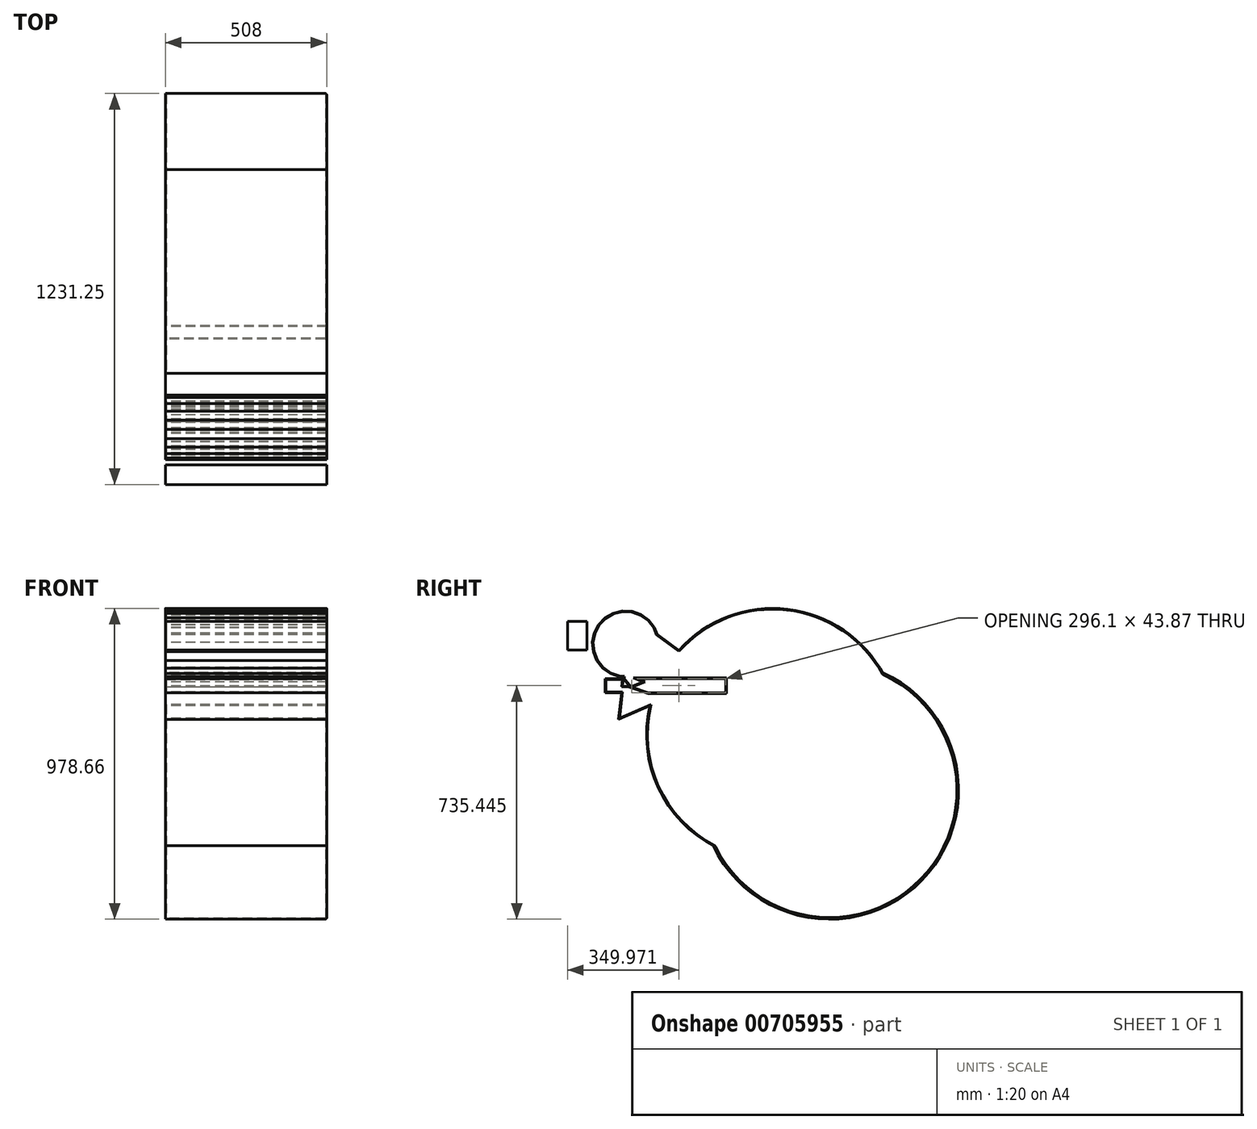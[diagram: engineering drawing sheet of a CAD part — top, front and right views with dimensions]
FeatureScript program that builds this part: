
annotation { "Feature Type Name" : "Feature", "Feature Type Description" : "" }
export const myFeature = defineFeature(function(context is Context, id is Id, definition is map)
    precondition{}
    {
        {
            var Q0;
            Q0=qCreatedBy(makeId("Right.planeOp"),FACE);
            var sketch = newSketch(context, id + "F0", { "sketchPlane" : qUnion([Q0])});
            skLineSegment(sketch, "E0.bottom", {"start": v(-498.02, 313) * mm, "end": v(-436.5, 313) * mm});
            skLineSegment(sketch, "E0.top", {"start": v(-498.02, 222.69) * mm, "end": v(-436.5, 222.69) * mm});
            skLineSegment(sketch, "E0.left", {"start": v(-498.02, 313) * mm, "end": v(-498.02, 222.69) * mm});
            skLineSegment(sketch, "E0.right", {"start": v(-436.5, 313) * mm, "end": v(-436.5, 222.69) * mm});
            skPoint(sketch, "E0.middle", {"position": v(-467.26, 267.84) * mm});
            skLineSegment(sketch, "E1.bottom", {"start": v(-379.5, 132.56) * mm, "end": v(0, 132.56) * mm});
            skLineSegment(sketch, "E1.top", {"start": v(-379.5, 88.69) * mm, "end": v(0, 88.69) * mm});
            skLineSegment(sketch, "E1.left", {"start": v(-379.5, 132.56) * mm, "end": v(-379.5, 88.69) * mm});
            skLineSegment(sketch, "E1.right", {"start": v(0, 132.56) * mm, "end": v(0, 88.69) * mm});
            skLineSegment(sketch, "E2.bottom", {"start": v(-302.6, 108.21) * mm, "end": v(-302.6, 108.21) * mm});
            skLineSegment(sketch, "E2.top", {"start": v(-302.6, 124.93) * mm, "end": v(-302.6, 124.93) * mm});
            skLineSegment(sketch, "E2.left", {"start": v(-302.6, 108.21) * mm, "end": v(-302.6, 124.93) * mm});
            skLineSegment(sketch, "E2.right", {"start": v(-302.6, 108.21) * mm, "end": v(-302.6, 124.93) * mm});
            skLineSegment(sketch, "E3", {"start": v(-379.5, 110.62) * mm, "end": v(-336.08, 110.62) * mm});
            skLineSegment(sketch, "E4", {"start": v(-336.08, 110.62) * mm, "end": v(-349.65, 132.56) * mm});
            skLineSegment(sketch, "E5", {"start": v(-336.08, 110.62) * mm, "end": v(-302.6, 108.21) * mm});
            skLineSegment(sketch, "E6", {"start": v(-302.6, 108.21) * mm, "end": v(-322.51, 132.56) * mm});
            skLineSegment(sketch, "E7", {"start": v(-302.6, 108.21) * mm, "end": v(-243.8, 88.69) * mm});
            skLineSegment(sketch, "E8", {"start": v(-296.1, 106.05) * mm, "end": v(-228.43, 132.56) * mm});
            skLineSegment(sketch, "E9", {"start": v(-277.04, 113.52) * mm, "end": v(-167.81, 88.69) * mm});
            skCircle(sketch, "E10.cCircle", {"center": v(-315.27, 241.47) * mm, "radius": 103.75 * mm, "construction": true});
            skLineSegment(sketch, "E10.0", {"start": v(-250.76, 158.85) * mm, "end": v(-276.65, 144.03) * mm});
            skLineSegment(sketch, "E10.1", {"start": v(-276.65, 144.03) * mm, "end": v(-305.67, 137.1) * mm});
            skLineSegment(sketch, "E10.2", {"start": v(-305.67, 137.1) * mm, "end": v(-335.46, 138.61) * mm});
            skLineSegment(sketch, "E10.3", {"start": v(-335.46, 138.61) * mm, "end": v(-363.62, 148.47) * mm});
            skLineSegment(sketch, "E10.4", {"start": v(-363.62, 148.47) * mm, "end": v(-387.87, 165.86) * mm});
            skLineSegment(sketch, "E10.5", {"start": v(-387.87, 165.86) * mm, "end": v(-406.23, 189.37) * mm});
            skLineSegment(sketch, "E10.6", {"start": v(-406.23, 189.37) * mm, "end": v(-417.22, 217.1) * mm});
            skLineSegment(sketch, "E10.7", {"start": v(-417.22, 217.1) * mm, "end": v(-419.95, 246.81) * mm});
            skLineSegment(sketch, "E10.8", {"start": v(-419.95, 246.81) * mm, "end": v(-414.2, 276.09) * mm});
            skLineSegment(sketch, "E10.9", {"start": v(-414.2, 276.09) * mm, "end": v(-400.45, 302.56) * mm});
            skLineSegment(sketch, "E10.10", {"start": v(-400.45, 302.56) * mm, "end": v(-379.78, 324.08) * mm});
            skLineSegment(sketch, "E10.11", {"start": v(-379.78, 324.08) * mm, "end": v(-353.9, 338.9) * mm});
            skLineSegment(sketch, "E10.12", {"start": v(-353.9, 338.9) * mm, "end": v(-324.88, 345.84) * mm});
            skLineSegment(sketch, "E10.13", {"start": v(-324.88, 345.84) * mm, "end": v(-295.08, 344.32) * mm});
            skLineSegment(sketch, "E10.14", {"start": v(-295.08, 344.32) * mm, "end": v(-266.93, 334.47) * mm});
            skLineSegment(sketch, "E10.15", {"start": v(-266.93, 334.47) * mm, "end": v(-242.68, 317.08) * mm});
            skLineSegment(sketch, "E10.16", {"start": v(-242.68, 317.08) * mm, "end": v(-224.32, 293.56) * mm});
            skLineSegment(sketch, "E10.17", {"start": v(-224.32, 293.56) * mm, "end": v(-213.33, 265.83) * mm});
            skLineSegment(sketch, "E10.18", {"start": v(-213.33, 265.83) * mm, "end": v(-210.6, 236.12) * mm});
            skLineSegment(sketch, "E10.19", {"start": v(-210.6, 236.12) * mm, "end": v(-216.34, 206.85) * mm});
            skLineSegment(sketch, "E10.20", {"start": v(-216.34, 206.85) * mm, "end": v(-230.1, 180.38) * mm});
            skLineSegment(sketch, "E10.21", {"start": v(-230.1, 180.38) * mm, "end": v(-250.76, 158.85) * mm});
            skPoint(sketch, "E10.0.midPoint", {"position": v(-263.7, 151.44) * mm});
            skCircle(sketch, "E11.cCircle", {"center": v(-223, 158.25) * mm, "radius": 95.8 * mm, "construction": true});
            skLineSegment(sketch, "E11.0", {"start": v(-32.68, 136.11) * mm, "end": v(-337.32, 4.5) * mm});
            skLineSegment(sketch, "E11.1", {"start": v(-337.32, 4.5) * mm, "end": v(-299, 334.13) * mm});
            skLineSegment(sketch, "E11.2", {"start": v(-299, 334.13) * mm, "end": v(-32.68, 136.11) * mm});
            skPoint(sketch, "E11.0.midPoint", {"position": v(-185, 70.3) * mm});
            skCircle(sketch, "E12", {"center": v(147.91, -43.4) * mm, "radius": 397.24 * mm});
            skCircle(sketch, "E13", {"center": v(327.03, -218.62) * mm, "radius": 406.2 * mm});
            skLineSegment(sketch, "E14", {"start": v(-419.31, 192.16) * mm, "end": v(-182.34, 91.99) * mm});
            skSolve(sketch);
        }
        {
            var Q0;
            Q0 = qSketchRegion(id + "F0", true);
            extrude(context, id + "F1", {"entities" : qUnion([Q0]), "depth" : 508 * mm, "offsetDistance" : 25.4 * mm});
        }
        {
            var Q0;
            Q0=makeQuery(id+"F1.opExtrude","CAP_EDGE",EDGE,{"disambiguationData":[OSD([sQuery(id+"F0.wireOp",EDGE,"E13")])],"isStart":false});
            fillet(context, id + "F2", {"entities" : qUnion([Q0]), "radius" : 5.08 * mm, "tangentPropagation" : true, "allowEdgeOverflow" : false});
        }
        {
            var Q0;
            Q0=makeQuery(id+"F1.opExtrude","CAP_FACE",FACE,{"disambiguationData":[OSD([sQuery(id+"F0.wireOp",EDGE,"E1.bottom"),sQuery(id+"F0.wireOp",EDGE,"E1.top"),sQuery(id+"F0.wireOp",EDGE,"E1.left"),sQuery(id+"F0.wireOp",EDGE,"E1.right"),sQuery(id+"F0.wireOp",EDGE,"E5"),sQuery(id+"F0.wireOp",EDGE,"E6"),sQuery(id+"F0.wireOp",EDGE,"E7"),sQuery(id+"F0.wireOp",EDGE,"E8"),sQuery(id+"F0.wireOp",EDGE,"E10.2"),sQuery(id+"F0.wireOp",EDGE,"E10.3"),sQuery(id+"F0.wireOp",EDGE,"E10.4"),sQuery(id+"F0.wireOp",EDGE,"E10.5"),sQuery(id+"F0.wireOp",EDGE,"E10.6"),sQuery(id+"F0.wireOp",EDGE,"E10.7"),sQuery(id+"F0.wireOp",EDGE,"E10.8"),sQuery(id+"F0.wireOp",EDGE,"E10.9"),sQuery(id+"F0.wireOp",EDGE,"E10.10"),sQuery(id+"F0.wireOp",EDGE,"E10.11"),sQuery(id+"F0.wireOp",EDGE,"E10.12"),sQuery(id+"F0.wireOp",EDGE,"E10.13"),sQuery(id+"F0.wireOp",EDGE,"E10.14"),sQuery(id+"F0.wireOp",EDGE,"E10.15"),sQuery(id+"F0.wireOp",EDGE,"E10.16"),sQuery(id+"F0.wireOp",EDGE,"E10.17"),sQuery(id+"F0.wireOp",EDGE,"E11.0"),sQuery(id+"F0.wireOp",EDGE,"E11.1"),sQuery(id+"F0.wireOp",EDGE,"E11.2"),sQuery(id+"F0.wireOp",EDGE,"E12"),sQuery(id+"F0.wireOp",EDGE,"E13"),sQuery(id+"F0.wireOp",EDGE,"E14")])],"isStart":false});
            shell(context, id + "F3", {"entities" : qUnion([Q0]), "thickness" : 2.54 * mm});
        }
    });
